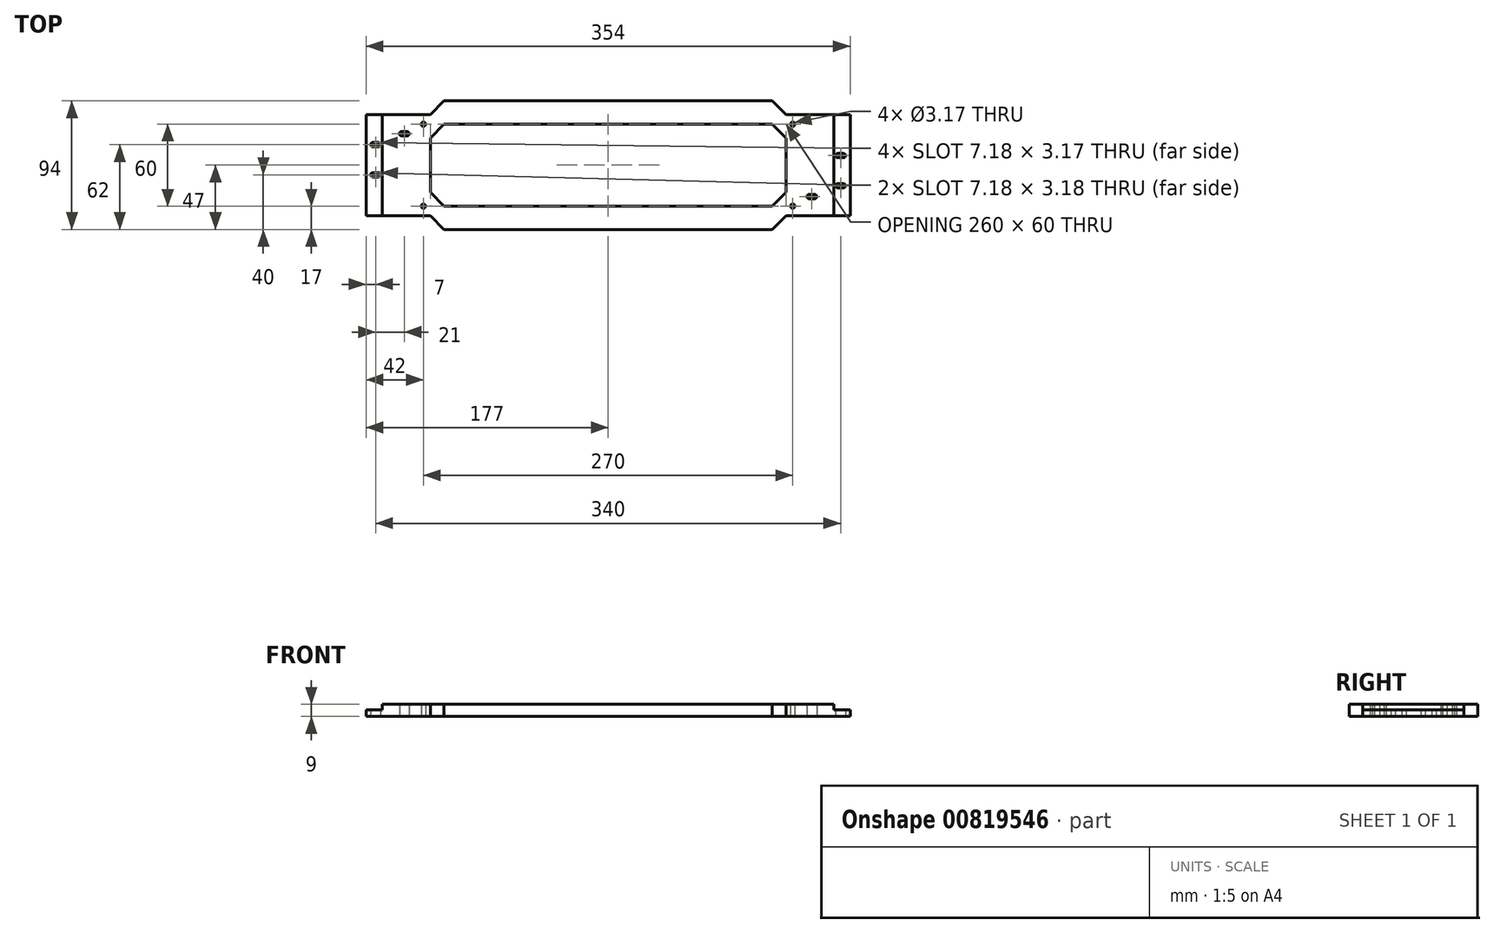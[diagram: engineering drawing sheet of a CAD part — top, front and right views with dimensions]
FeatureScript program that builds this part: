
annotation { "Feature Type Name" : "Feature", "Feature Type Description" : "" }
export const myFeature = defineFeature(function(context is Context, id is Id, definition is map)
    precondition{}
    {
        {
            var Q0;
            Q0=qCreatedBy(makeId("Top.planeOp"),FACE);
            var sketch = newSketch(context, id + "F0", { "sketchPlane" : qUnion([Q0])});
            skLineSegment(sketch, "E0.bottom", {"start": v(177, 37) * mm, "end": v(130, 37) * mm});
            skLineSegment(sketch, "E0.top", {"start": v(177, -37) * mm, "end": v(130, -37) * mm});
            skLineSegment(sketch, "E0.left", {"start": v(177, 37) * mm, "end": v(177, -37) * mm});
            skLineSegment(sketch, "E0.right", {"start": v(-177, 37) * mm, "end": v(-177, -37) * mm});
            skPoint(sketch, "E0.middle", {"position": v(0, 0) * mm});
            skCircle(sketch, "E1", {"center": v(-135, -30) * mm, "radius": 1.59 * mm});
            skCircle(sketch, "E2.MirrorC", {"center": v(135, -30) * mm, "radius": 1.59 * mm});
            skCircle(sketch, "E3.MirrorC", {"center": v(-135, 30) * mm, "radius": 1.59 * mm});
            skCircle(sketch, "E4.MirrorC", {"center": v(135, 30) * mm, "radius": 1.59 * mm});
            skLineSegment(sketch, "E5.left", {"start": v(130, 20) * mm, "end": v(130, -20) * mm});
            skLineSegment(sketch, "E5.right", {"start": v(-130, 20) * mm, "end": v(-130, -20) * mm});
            skLineSegment(sketch, "E6", {"start": v(-172, 15) * mm, "end": v(-168, 15) * mm, "construction": true});
            skLineSegment(sketch, "E7", {"start": v(-172, -7) * mm, "end": v(-168, -7) * mm, "construction": true});
            skArc(sketch, "E8.0.startCap", {"start": v(-172, 13.41) * mm, "mid": v(-173.59, 15) * mm, "end": v(-172, 16.59) * mm});
            skArc(sketch, "E8.0.endCap", {"start": v(-168, 16.59) * mm, "mid": v(-166.41, 15) * mm, "end": v(-168, 13.41) * mm});
            skLineSegment(sketch, "E8.0.left", {"start": v(-172, 16.59) * mm, "end": v(-168, 16.59) * mm});
            skLineSegment(sketch, "E8.0.right", {"start": v(-172, 13.41) * mm, "end": v(-168, 13.41) * mm});
            skArc(sketch, "E9.0.startCap", {"start": v(-172, -8.59) * mm, "mid": v(-173.59, -7) * mm, "end": v(-172, -5.41) * mm});
            skArc(sketch, "E9.0.endCap", {"start": v(-168, -5.41) * mm, "mid": v(-166.41, -7) * mm, "end": v(-168, -8.59) * mm});
            skLineSegment(sketch, "E9.0.left", {"start": v(-172, -5.41) * mm, "end": v(-168, -5.41) * mm});
            skLineSegment(sketch, "E9.0.right", {"start": v(-172, -8.59) * mm, "end": v(-168, -8.59) * mm});
            skLineSegment(sketch, "E10", {"start": v(-151, 23) * mm, "end": v(-147, 23) * mm, "construction": true});
            skPoint(sketch, "E11", {"position": v(-149, 23) * mm});
            skArc(sketch, "E12.0.startCap", {"start": v(-151, 21.41) * mm, "mid": v(-152.59, 23) * mm, "end": v(-151, 24.59) * mm});
            skArc(sketch, "E12.0.endCap", {"start": v(-147, 24.59) * mm, "mid": v(-145.41, 23) * mm, "end": v(-147, 21.41) * mm});
            skLineSegment(sketch, "E12.0.left", {"start": v(-151, 24.59) * mm, "end": v(-147, 24.59) * mm});
            skLineSegment(sketch, "E12.0.right", {"start": v(-151, 21.41) * mm, "end": v(-147, 21.41) * mm});
            skPoint(sketch, "E13", {"position": v(-170, -7) * mm});
            skLineSegment(sketch, "E14", {"start": v(172, -15) * mm, "end": v(168, -15) * mm, "construction": true});
            skLineSegment(sketch, "E15", {"start": v(172, 7) * mm, "end": v(168, 7) * mm, "construction": true});
            skArc(sketch, "E16.0.startCap", {"start": v(172, -13.41) * mm, "mid": v(173.59, -15) * mm, "end": v(172, -16.59) * mm});
            skArc(sketch, "E16.0.endCap", {"start": v(168, -16.59) * mm, "mid": v(166.41, -15) * mm, "end": v(168, -13.41) * mm});
            skLineSegment(sketch, "E16.0.left", {"start": v(172, -16.59) * mm, "end": v(168, -16.59) * mm});
            skLineSegment(sketch, "E16.0.right", {"start": v(172, -13.41) * mm, "end": v(168, -13.41) * mm});
            skArc(sketch, "E17.0.startCap", {"start": v(172, 8.59) * mm, "mid": v(173.59, 7) * mm, "end": v(172, 5.41) * mm});
            skArc(sketch, "E17.0.endCap", {"start": v(168, 5.41) * mm, "mid": v(166.41, 7) * mm, "end": v(168, 8.59) * mm});
            skLineSegment(sketch, "E17.0.left", {"start": v(172, 5.41) * mm, "end": v(168, 5.41) * mm});
            skLineSegment(sketch, "E17.0.right", {"start": v(172, 8.59) * mm, "end": v(168, 8.59) * mm});
            skLineSegment(sketch, "E18", {"start": v(151, -23) * mm, "end": v(147, -23) * mm, "construction": true});
            skPoint(sketch, "E19", {"position": v(149, -23) * mm});
            skArc(sketch, "E20.0.startCap", {"start": v(151, -21.41) * mm, "mid": v(152.59, -23) * mm, "end": v(151, -24.59) * mm});
            skArc(sketch, "E20.0.endCap", {"start": v(147, -24.59) * mm, "mid": v(145.41, -23) * mm, "end": v(147, -21.41) * mm});
            skLineSegment(sketch, "E20.0.left", {"start": v(151, -24.59) * mm, "end": v(147, -24.59) * mm});
            skLineSegment(sketch, "E20.0.right", {"start": v(151, -21.41) * mm, "end": v(147, -21.41) * mm});
            skPoint(sketch, "E21", {"position": v(170, 7) * mm});
            skLineSegment(sketch, "E22", {"start": v(-120, -30) * mm, "end": v(120, -30) * mm});
            skLineSegment(sketch, "E23", {"start": v(120, 30) * mm, "end": v(-120, 30) * mm});
            skLineSegment(sketch, "E24", {"start": v(-130, 20) * mm, "end": v(-120, 30) * mm});
            skLineSegment(sketch, "E25", {"start": v(-130, -20) * mm, "end": v(-120, -30) * mm});
            skLineSegment(sketch, "E26", {"start": v(120, -30) * mm, "end": v(130, -20) * mm});
            skLineSegment(sketch, "E27", {"start": v(130, 20) * mm, "end": v(120, 30) * mm});
            skLineSegment(sketch, "E28", {"start": v(-120, 47) * mm, "end": v(120, 47) * mm});
            skLineSegment(sketch, "E29", {"start": v(-120, 47) * mm, "end": v(-130, 37) * mm});
            skLineSegment(sketch, "E30.MirrorCS", {"start": v(120, 47) * mm, "end": v(130, 37) * mm});
            skLineSegment(sketch, "E31.trimOffspring", {"start": v(-130, 37) * mm, "end": v(-177, 37) * mm});
            skLineSegment(sketch, "E32.MirrorCS", {"start": v(-120, -47) * mm, "end": v(-130, -37) * mm});
            skLineSegment(sketch, "E33.MirrorCS", {"start": v(-120, -47) * mm, "end": v(120, -47) * mm});
            skLineSegment(sketch, "E34.MirrorCS", {"start": v(120, -47) * mm, "end": v(130, -37) * mm});
            skLineSegment(sketch, "E35.trimOffspring", {"start": v(-130, -37) * mm, "end": v(-177, -37) * mm});
            skSolve(sketch);
        }
        {
            var Q0;
            Q0=makeQuery(id+"F0.imprint","IMPRINT",FACE,{"disambiguationData":[TD([[makeQuery(id+"F0.imprint","IMPRINT",EDGE,{"derivedFrom":sQuery(id+"F0.wireOp",EDGE,"E0.bottom")}),1.0]])]});
            extrude(context, id + "F1", {"entities" : qUnion([Q0]), "depth" : 9 * mm, "offsetDistance" : 25 * mm});
        }
        {
            var Q0;
            Q0=qCreatedBy(makeId("Front.planeOp"),FACE);
            var sketch = newSketch(context, id + "F2", { "sketchPlane" : qUnion([Q0])});
            skCircle(sketch, "E36", {"center": v(-208, 9) * mm, "radius": 6 * mm});
            skSolve(sketch);
        }
        {
            var Q0;
            Q0=makeQuery(id+"F1.opExtrude","CAP_FACE",FACE,{"disambiguationData":[OSD([sQuery(id+"F0.wireOp",EDGE,"E0.bottom"),sQuery(id+"F0.wireOp",EDGE,"E0.top"),sQuery(id+"F0.wireOp",EDGE,"E0.left"),sQuery(id+"F0.wireOp",EDGE,"E0.right"),sQuery(id+"F0.wireOp",EDGE,"E1"),sQuery(id+"F0.wireOp",EDGE,"E2.MirrorC"),sQuery(id+"F0.wireOp",EDGE,"E3.MirrorC"),sQuery(id+"F0.wireOp",EDGE,"E4.MirrorC"),sQuery(id+"F0.wireOp",EDGE,"E5.bottom"),sQuery(id+"F0.wireOp",EDGE,"E5.top"),sQuery(id+"F0.wireOp",EDGE,"E5.left"),sQuery(id+"F0.wireOp",EDGE,"E5.right"),sQuery(id+"F0.wireOp",EDGE,"E8.0.startCap"),sQuery(id+"F0.wireOp",EDGE,"E8.0.endCap"),sQuery(id+"F0.wireOp",EDGE,"E8.0.left"),sQuery(id+"F0.wireOp",EDGE,"E8.0.right"),sQuery(id+"F0.wireOp",EDGE,"E9.0.startCap"),sQuery(id+"F0.wireOp",EDGE,"E9.0.endCap"),sQuery(id+"F0.wireOp",EDGE,"E9.0.left"),sQuery(id+"F0.wireOp",EDGE,"E9.0.right"),sQuery(id+"F0.wireOp",EDGE,"E12.0.startCap"),sQuery(id+"F0.wireOp",EDGE,"E12.0.endCap"),sQuery(id+"F0.wireOp",EDGE,"E12.0.left"),sQuery(id+"F0.wireOp",EDGE,"E12.0.right"),sQuery(id+"F0.wireOp",EDGE,"E16.0.startCap"),sQuery(id+"F0.wireOp",EDGE,"E16.0.endCap"),sQuery(id+"F0.wireOp",EDGE,"E16.0.left"),sQuery(id+"F0.wireOp",EDGE,"E16.0.right"),sQuery(id+"F0.wireOp",EDGE,"E17.0.startCap"),sQuery(id+"F0.wireOp",EDGE,"E17.0.endCap"),sQuery(id+"F0.wireOp",EDGE,"E17.0.left"),sQuery(id+"F0.wireOp",EDGE,"E17.0.right"),sQuery(id+"F0.wireOp",EDGE,"E20.0.startCap"),sQuery(id+"F0.wireOp",EDGE,"E20.0.endCap"),sQuery(id+"F0.wireOp",EDGE,"E20.0.left"),sQuery(id+"F0.wireOp",EDGE,"E20.0.right")])],"isStart":false});
            var sketch = newSketch(context, id + "F3", { "sketchPlane" : qUnion([Q0])});
            skLineSegment(sketch, "E37", {"start": v(-165, 37) * mm, "end": v(-165, -37) * mm});
            skLineSegment(sketch, "E38.MirrorCS", {"start": v(165, 37) * mm, "end": v(165, -37) * mm});
            skSolve(sketch);
        }
        {
            var Q0;
            {var subQ2=sQuery(id+"F3.wireOp",EDGE,"E37");Q0=makeQuery(id+"F3.imprint","IMPRINT",FACE,{"disambiguationData":[TD([[makeQuery(id+"F3.imprint","IMPRINT",EDGE,{"derivedFrom":subQ2}),-1.0]])]});}
            var Q1;
            {var subQ0=sQuery(id+"F3.wireOp",EDGE,"E38.MirrorCS");Q1=makeQuery(id+"F3.imprint","IMPRINT",FACE,{"disambiguationData":[TD([[makeQuery(id+"F3.imprint","IMPRINT",EDGE,{"derivedFrom":subQ0}),1.0]])]});}
            extrude(context, id + "F4", {"entities" : qUnion([Q0, Q1]), "operationType" : NewBodyOperationType.REMOVE, "oppositeDirection" : true, "depth" : 4 * mm, "offsetDistance" : 25 * mm});
        }
    });
